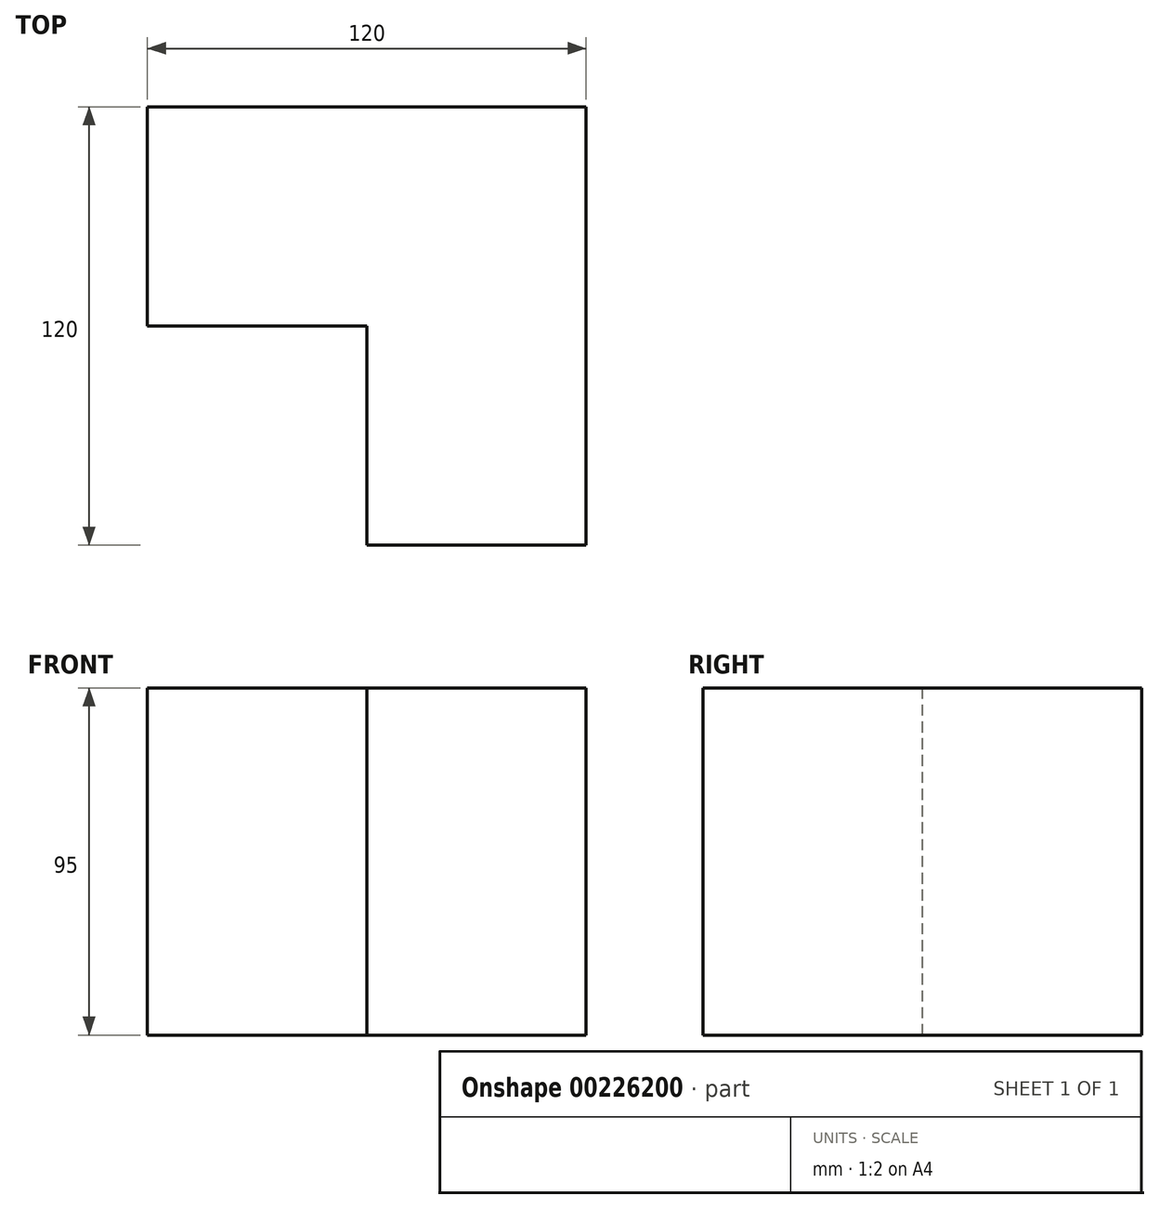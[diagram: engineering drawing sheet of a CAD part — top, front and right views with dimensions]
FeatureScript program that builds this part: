
annotation { "Feature Type Name" : "Feature", "Feature Type Description" : "" }
export const myFeature = defineFeature(function(context is Context, id is Id, definition is map)
    precondition{}
    {
        {
            var Q0;
            Q0=qCreatedBy(makeId("Top.planeOp"),FACE);
            var sketch = newSketch(context, id + "F0", { "sketchPlane" : qUnion([Q0])});
            skLineSegment(sketch, "E0.bottom", {"start": v(0, 0) * mm, "end": v(-120, 0) * mm});
            skLineSegment(sketch, "E0.top", {"start": v(0, -120) * mm, "end": v(-60, -120) * mm});
            skLineSegment(sketch, "E0.left", {"start": v(0, 0) * mm, "end": v(0, -120) * mm});
            skLineSegment(sketch, "E0.right", {"start": v(-120, 0) * mm, "end": v(-120, -60) * mm});
            skLineSegment(sketch, "E1.top", {"start": v(-120, -60) * mm, "end": v(-60, -60) * mm});
            skLineSegment(sketch, "E1.right", {"start": v(-60, -120) * mm, "end": v(-60, -60) * mm});
            skSolve(sketch);
        }
        {
            var Q0;
            Q0=makeQuery(id+"F0.imprint","IMPRINT",FACE,{"disambiguationData":[TD([[makeQuery(id+"F0.imprint","IMPRINT",EDGE,{"derivedFrom":sQuery(id+"F0.wireOp",EDGE,"E0.bottom")}),1.0]])]});
            extrude(context, id + "F1", {"entities" : qUnion([Q0]), "oppositeDirection" : true, "depth" : 95 * mm});
        }
    });
